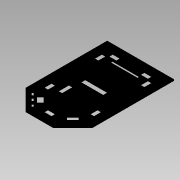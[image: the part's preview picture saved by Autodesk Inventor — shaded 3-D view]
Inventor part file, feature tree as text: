
AUTODESK INVENTOR PART (.ipt)
format: ipt  version: 2015 SP1 (Build 190203100, 203)  size: 332,800 bytes
history: native  units: mm
features: extrude x1, sketch x1
ambient origin geometry x8: Origin, YZ Plane, XZ Plane, XY Plane, X Axis, Y Axis, Z Axis, Center Point
bodies: Body1 (feature_tree)
feature tree (2):
  extrude  "Extrusion3"  Depth=140.811657mm
  sketch  "Sketch1"  dims[d104=30.0mm d106=23.0mm d107=30.0mm d109=23.0mm d121=172.234468mm d122=140.811657mm d123=172.234468mm d124=58.326098mm d125=58.326098mm d126=58.326098mm d127=23.561995mm d128=23.561874mm d129=23.562018mm d130=23.561892mm d131=15.707985mm d132=15.707942mm d134=8.999361mm d135=8.999879mm d138=9.0mm d146=3.0mm d147=3.0mm d148=3.0mm d152=3.0mm d153=3.0mm d154=3.0mm d158=3.0mm d184=15.0mm d185=3.0mm d186=30.0mm d188=23.0mm d189=30.0mm d191=23.0mm d194=3.0mm d195=0.0mm]
